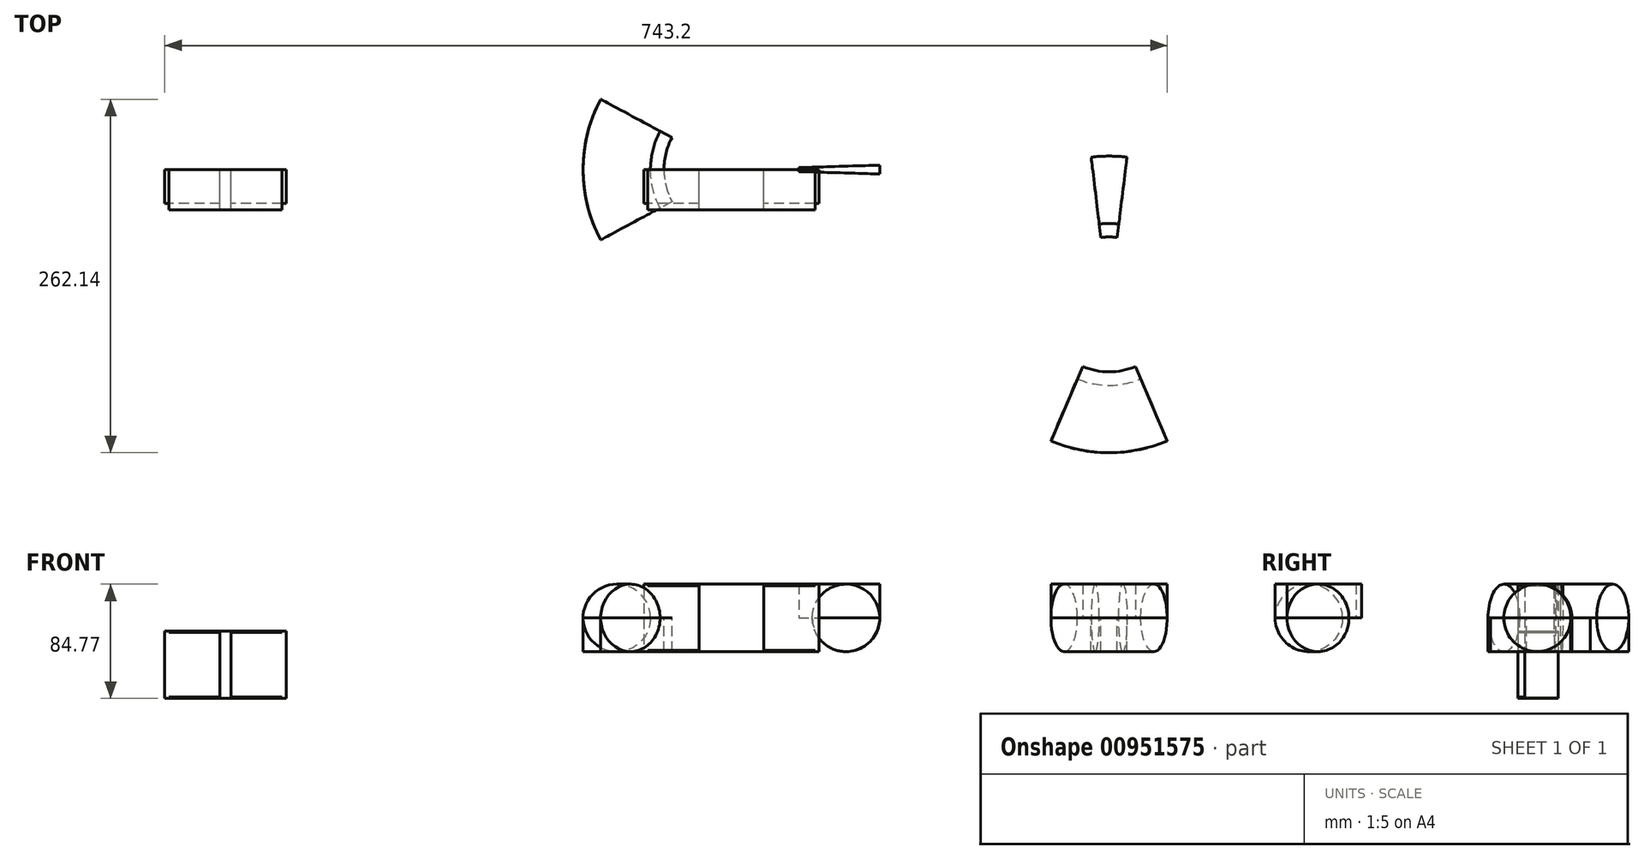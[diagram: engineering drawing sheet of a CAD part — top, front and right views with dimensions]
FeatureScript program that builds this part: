
annotation { "Feature Type Name" : "Feature", "Feature Type Description" : "" }
export const myFeature = defineFeature(function(context is Context, id is Id, definition is map)
    precondition{}
    {
        {
            var Q0;
            Q0=qCreatedBy(makeId("Top.planeOp"),FACE);
            var sketch = newSketch(context, id + "F0", { "sketchPlane" : qUnion([Q0])});
            skCircle(sketch, "E0", {"center": v(0, 0) * mm, "radius": 110 * mm});
            skLineSegment(sketch, "E1", {"start": v(0, 0) * mm, "end": v(-143.93, 0) * mm, "construction": true});
            skLineSegment(sketch, "E2", {"start": v(0, 0) * mm, "end": v(0, 124.12) * mm, "construction": true});
            skCircle(sketch, "E3", {"center": v(0, 0) * mm, "radius": 50 * mm});
            skLineSegment(sketch, "E4", {"start": v(0, 0) * mm, "end": v(109.95, 3.28) * mm});
            skLineSegment(sketch, "E5", {"start": v(0, 0) * mm, "end": v(-96.86, 52.14) * mm});
            skLineSegment(sketch, "E6", {"start": v(0, 0) * mm, "end": v(20.7, 87.59) * mm, "construction": true});
            skCircle(sketch, "E7", {"center": v(20.7, 87.59) * mm, "radius": 8 * mm});
            skCircle(sketch, "E8", {"center": v(190, 90) * mm, "radius": 23.3 * mm, "construction": true});
            skCircle(sketch, "E9", {"center": v(210.17, 101.65) * mm, "radius": 9.5 * mm});
            skLineSegment(sketch, "E10", {"start": v(20.7, 87.59) * mm, "end": v(210.17, 101.65) * mm, "construction": true});
            skLineSegment(sketch, "E11", {"start": v(210.17, 101.65) * mm, "end": v(190, 90) * mm});
            skLineSegment(sketch, "E12", {"start": v(190, -100) * mm, "end": v(280, -100) * mm, "construction": true});
            skCircle(sketch, "E13", {"center": v(280, -100) * mm, "radius": 110 * mm});
            skLineSegment(sketch, "E14", {"start": v(210.17, 101.65) * mm, "end": v(190.9, -87.37) * mm, "construction": true});
            skCircle(sketch, "E15", {"center": v(280, -100) * mm, "radius": 90 * mm, "construction": true});
            skCircle(sketch, "E16", {"center": v(0, 0) * mm, "radius": 90 * mm, "construction": true});
            skLineSegment(sketch, "E17", {"start": v(190.9, -87.37) * mm, "end": v(280, -100) * mm, "construction": true});
            skCircle(sketch, "E18", {"center": v(280, -100) * mm, "radius": 50 * mm});
            skCircle(sketch, "E19", {"center": v(20.7, 87.59) * mm, "radius": 23.3 * mm, "construction": true});
            skLineSegment(sketch, "E20", {"start": v(0, 0) * mm, "end": v(-2.51, 84.3) * mm, "construction": true});
            skLineSegment(sketch, "E21", {"start": v(0, 0) * mm, "end": v(41.46, 77.02) * mm, "construction": true});
            skCircle(sketch, "E22", {"center": v(190.9, -87.37) * mm, "radius": 23.3 * mm, "construction": true});
            skLineSegment(sketch, "E23", {"start": v(280, -100) * mm, "end": v(266.72, 9.2) * mm});
            skLineSegment(sketch, "E24", {"start": v(280, -100) * mm, "end": v(236.9, -201.2) * mm});
            skLineSegment(sketch, "E25", {"start": v(190, 90) * mm, "end": v(0, 90) * mm, "construction": true});
            skCircle(sketch, "E26", {"center": v(190.9, -87.37) * mm, "radius": 8 * mm});
            skLineSegment(sketch, "E27", {"start": v(190, 90) * mm, "end": v(190, -203.4) * mm, "construction": true});
            skLineSegment(sketch, "E28", {"start": v(0, 0) * mm, "end": v(-96.86, -52.14) * mm});
            skLineSegment(sketch, "E29", {"start": v(0, 0) * mm, "end": v(109.95, -3.28) * mm});
            skLineSegment(sketch, "E30", {"start": v(0, 0) * mm, "end": v(20.7, -87.59) * mm, "construction": true});
            skLineSegment(sketch, "E31", {"start": v(280, -100) * mm, "end": v(293.28, 9.2) * mm});
            skLineSegment(sketch, "E32", {"start": v(280, -100) * mm, "end": v(323.1, -201.2) * mm});
            skLineSegment(sketch, "E33", {"start": v(280, -100) * mm, "end": v(369.1, -87.37) * mm, "construction": true});
            skLineSegment(sketch, "E34", {"start": v(280, -100) * mm, "end": v(280, 59.02) * mm, "construction": true});
            skLineSegment(sketch, "E35", {"start": v(110, 0) * mm, "end": v(246.79, 69.95) * mm, "construction": true});
            skLineSegment(sketch, "E36", {"start": v(246.79, 69.95) * mm, "end": v(280, 10) * mm, "construction": true});
            skLineSegment(sketch, "E37", {"start": v(-110, 0) * mm, "end": v(-201, -57.62) * mm, "construction": true});
            skLineSegment(sketch, "E38", {"start": v(-201, -57.62) * mm, "end": v(-128.27, -241.78) * mm, "construction": true});
            skLineSegment(sketch, "E39", {"start": v(-128.27, -241.78) * mm, "end": v(280, -241.78) * mm, "construction": true});
            skLineSegment(sketch, "E40", {"start": v(280, -241.78) * mm, "end": v(280, -210) * mm, "construction": true});
            skSolve(sketch);
        }
        {
            var Q0;
            {var subQ0=sQuery(id+"F0.wireOp",EDGE,"E4");var subQ1=sQuery(id+"F0.wireOp",EDGE,"E0");var subQ2=makeQuery(id+"F0.imprint","INTERSECT",VERTEX,{"derivedFrom":[subQ1,subQ0]});Q0=makeQuery(id+"F0.imprint","IMPRINT",FACE,{"disambiguationData":[TD([[makeQuery(id+"F0.imprint","IMPRINT",EDGE,{"disambiguationData":[TD([[subQ2,1.0]])],"derivedFrom":subQ1}),1.0]])]});}
            var Q1;
            {var subQ0=sQuery(id+"F0.wireOp",EDGE,"E24");var subQ1=sQuery(id+"F0.wireOp",EDGE,"E13");var subQ2=makeQuery(id+"F0.imprint","INTERSECT",VERTEX,{"derivedFrom":[subQ1,subQ0]});Q1=makeQuery(id+"F0.imprint","IMPRINT",FACE,{"disambiguationData":[TD([[makeQuery(id+"F0.imprint","IMPRINT",EDGE,{"disambiguationData":[TD([[subQ2,-1.0]])],"derivedFrom":subQ1}),1.0]])]});}
            extrude(context, id + "F1", {"entities" : qUnion([Q0, Q1]), "depth" : 25 * mm, "offsetDistance" : 25 * mm});
        }
        {
            var Q0;
            {var subQ0=sQuery(id+"F0.wireOp",EDGE,"E5");var subQ1=sQuery(id+"F0.wireOp",EDGE,"E0");var subQ2=makeQuery(id+"F0.imprint","INTERSECT",VERTEX,{"derivedFrom":[subQ1,subQ0]});Q0=makeQuery(id+"F0.imprint","IMPRINT",FACE,{"disambiguationData":[TD([[makeQuery(id+"F0.imprint","IMPRINT",EDGE,{"disambiguationData":[TD([[subQ2,-1.0]])],"derivedFrom":subQ1}),1.0]])]});}
            var Q1;
            {var subQ0=sQuery(id+"F0.wireOp",EDGE,"E23");var subQ1=sQuery(id+"F0.wireOp",EDGE,"E13");var subQ2=makeQuery(id+"F0.imprint","INTERSECT",VERTEX,{"derivedFrom":[subQ1,subQ0]});Q1=makeQuery(id+"F0.imprint","IMPRINT",FACE,{"disambiguationData":[TD([[makeQuery(id+"F0.imprint","IMPRINT",EDGE,{"disambiguationData":[TD([[subQ2,1.0]])],"derivedFrom":subQ1}),1.0]])]});}
            extrude(context, id + "F2", {"entities" : qUnion([Q0, Q1]), "oppositeDirection" : true, "depth" : 25 * mm, "offsetDistance" : 25 * mm});
        }
        {
            var Q0;
            Q0=qCreatedBy(makeId("Front.planeOp"),FACE);
            var sketch = newSketch(context, id + "F3", { "sketchPlane" : qUnion([Q0])});
            skLineSegment(sketch, "E41", {"start": v(0, 0) * mm, "end": v(0, 86.34) * mm});
            skCircle(sketch, "E42", {"center": v(-85, 0) * mm, "radius": 25 * mm});
            skLineSegment(sketch, "E43", {"start": v(0, 0) * mm, "end": v(123.31, 0) * mm});
            skPoint(sketch, "E44", {"position": v(-110, 0) * mm});
            skSolve(sketch);
        }
        {
            var Q0;
            Q0=makeQuery(id+"F3.imprint","IMPRINT",FACE,{"disambiguationData":[TD([[makeQuery(id+"F3.imprint","IMPRINT",EDGE,{"derivedFrom":sQuery(id+"F3.wireOp",EDGE,"E42")}),1.0]])]});
            var Q1;
            Q1=sQuery(id+"F3.wireOp",EDGE,"E41");
            revolve(context, id + "F4", {"surfaceOperationType" : NewSurfaceOperationType.NEW, "entities" : qUnion([Q0]), "axis" : qUnion([Q1]), "revolveType" : RevolveType.FULL});
        }
        {
            var Q0;
            {var subQ0=sQuery(id+"F0.wireOp",EDGE,"E28");var subQ1=sQuery(id+"F0.wireOp",EDGE,"E0");var subQ2=makeQuery(id+"F0.imprint","INTERSECT",VERTEX,{"derivedFrom":[subQ1,subQ0]});Q0=makeQuery(id+"F0.imprint","IMPRINT",FACE,{"disambiguationData":[TD([[makeQuery(id+"F0.imprint","IMPRINT",EDGE,{"disambiguationData":[TD([[subQ2,-1.0]])],"derivedFrom":subQ1}),1.0]])]});}
            var Q1;
            Q1=makeQuery(id+"F0.imprint","IMPRINT",FACE,{"disambiguationData":[TD([[makeQuery(id+"F0.imprint","IMPRINT",EDGE,{"derivedFrom":sQuery(id+"F0.wireOp",EDGE,"E7")}),-1.0]])]});
            var Q2;
            Q2=makeQuery(id+"F0.imprint","IMPRINT",FACE,{"disambiguationData":[TD([[makeQuery(id+"F0.imprint","IMPRINT",EDGE,{"derivedFrom":sQuery(id+"F0.wireOp",EDGE,"E7")}),1.0]])]});
            extrude(context, id + "F5", {"entities" : qUnion([Q0, Q1, Q2]), "operationType" : NewBodyOperationType.REMOVE, "endBound" : BoundingType.SYMMETRIC, "depth" : 800 * mm, "offsetDistance" : 25 * mm});
        }
        {
            var Q0;
            Q0=qCreatedBy(makeId("Right.planeOp"),FACE);
            var Q1;
            Q1=sQuery(id+"F0.wireOp",VERTEX,"E36.end");
            cPlane(context, id + "F6", {"entities" : qUnion([Q0, Q1]), "cplaneType" : CPlaneType.PLANE_POINT, "offset" : 25 * mm, "width" : 150 * mm, "height" : 150 * mm});
        }
        {
            var Q0;
            Q0=qCreatedBy(id+"F6.planeOp",FACE);
            var sketch = newSketch(context, id + "F7", { "sketchPlane" : qUnion([Q0])});
            skLineSegment(sketch, "E45", {"start": v(-100, 70.8) * mm, "end": v(-100, 0) * mm});
            skCircle(sketch, "E46", {"center": v(-15, 0) * mm, "radius": 25 * mm});
            skLineSegment(sketch, "E47", {"start": v(-15, 0) * mm, "end": v(10, 0) * mm, "construction": true});
            skLineSegment(sketch, "E48", {"start": v(-100, 0) * mm, "end": v(-330.04, 0) * mm});
            skSolve(sketch);
        }
        {
            var Q0;
            Q0=makeQuery(id+"F7.imprint","IMPRINT",FACE,{"disambiguationData":[TD([[makeQuery(id+"F7.imprint","IMPRINT",EDGE,{"derivedFrom":sQuery(id+"F7.wireOp",EDGE,"E46")}),1.0]])]});
            var Q1;
            Q1=sQuery(id+"F7.wireOp",EDGE,"E45");
            revolve(context, id + "F8", {"surfaceOperationType" : NewSurfaceOperationType.NEW, "entities" : qUnion([Q0]), "axis" : qUnion([Q1]), "revolveType" : RevolveType.FULL});
        }
        {
            var Q0;
            {var subQ0=sQuery(id+"F0.wireOp",EDGE,"E31");var subQ1=sQuery(id+"F0.wireOp",EDGE,"E13");var subQ2=makeQuery(id+"F0.imprint","INTERSECT",VERTEX,{"derivedFrom":[subQ1,subQ0]});Q0=makeQuery(id+"F0.imprint","IMPRINT",FACE,{"disambiguationData":[TD([[makeQuery(id+"F0.imprint","IMPRINT",EDGE,{"disambiguationData":[TD([[subQ2,1.0]])],"derivedFrom":subQ1}),1.0]])]});}
            var Q1;
            Q1=makeQuery(id+"F0.imprint","IMPRINT",FACE,{"disambiguationData":[TD([[makeQuery(id+"F0.imprint","IMPRINT",EDGE,{"derivedFrom":sQuery(id+"F0.wireOp",EDGE,"E26")}),-1.0]])]});
            var Q2;
            Q2=makeQuery(id+"F0.imprint","IMPRINT",FACE,{"disambiguationData":[TD([[makeQuery(id+"F0.imprint","IMPRINT",EDGE,{"derivedFrom":sQuery(id+"F0.wireOp",EDGE,"E26")}),1.0]])]});
            extrude(context, id + "F9", {"entities" : qUnion([Q0, Q1, Q2]), "operationType" : NewBodyOperationType.REMOVE, "endBound" : BoundingType.SYMMETRIC, "depth" : 800 * mm, "offsetDistance" : 25 * mm});
        }
        {
            var Q0;
            Q0=qCreatedBy(makeId("Front.planeOp"),FACE);
            var sketch = newSketch(context, id + "F10", { "sketchPlane" : qUnion([Q0])});
            skLineSegment(sketch, "E49.bottom", {"start": v(-65, 25) * mm, "end": v(65, 25) * mm});
            skLineSegment(sketch, "E49.top", {"start": v(-65, -25) * mm, "end": v(65, -25) * mm});
            skLineSegment(sketch, "E49.left", {"start": v(-65, 25) * mm, "end": v(-65, -25) * mm});
            skLineSegment(sketch, "E49.right", {"start": v(65, 25) * mm, "end": v(65, -25) * mm});
            skPoint(sketch, "E49.middle", {"position": v(0, 0) * mm});
            skLineSegment(sketch, "E50", {"start": v(-62, 25) * mm, "end": v(-62, 24) * mm});
            skLineSegment(sketch, "E51", {"start": v(-62, 24) * mm, "end": v(-24, 24) * mm});
            skLineSegment(sketch, "E52", {"start": v(-24, 24) * mm, "end": v(-24, -24) * mm});
            skLineSegment(sketch, "E53", {"start": v(0, 0) * mm, "end": v(40.86, 0) * mm});
            skLineSegment(sketch, "E54", {"start": v(0, 0) * mm, "end": v(0, 32.58) * mm});
            skLineSegment(sketch, "E55", {"start": v(-24, -24) * mm, "end": v(-62, -24) * mm});
            skLineSegment(sketch, "E56", {"start": v(-62, -24) * mm, "end": v(-62, -25) * mm});
            skLineSegment(sketch, "E57.MirrorCS", {"start": v(62, 25) * mm, "end": v(62, 24) * mm});
            skLineSegment(sketch, "E58.MirrorCS", {"start": v(62, 24) * mm, "end": v(24, 24) * mm});
            skLineSegment(sketch, "E59.MirrorCS", {"start": v(24, 24) * mm, "end": v(24, -24) * mm});
            skLineSegment(sketch, "E60.MirrorCS", {"start": v(24, -24) * mm, "end": v(62, -24) * mm});
            skLineSegment(sketch, "E61.MirrorCS", {"start": v(62, -24) * mm, "end": v(62, -25) * mm});
            skLineSegment(sketch, "E62", {"start": v(0, 29.12) * mm, "end": v(-2.43, 29.12) * mm});
            skLineSegment(sketch, "E63", {"start": v(-3, 40) * mm, "end": v(-4, 40) * mm});
            skLineSegment(sketch, "E64", {"start": v(-4, 40) * mm, "end": v(-4.57, 29.12) * mm});
            skLineSegment(sketch, "E65", {"start": v(-3.5, 43.91) * mm, "end": v(-3.5, 28.26) * mm, "construction": true});
            skPoint(sketch, "E66.orphan", {"position": v(-3.5, 40) * mm});
            skLineSegment(sketch, "E67.MirrorCS", {"start": v(-3, 40) * mm, "end": v(-2.43, 29.12) * mm});
            skLineSegment(sketch, "E68", {"start": v(-4.57, 29.12) * mm, "end": v(-7, 29.12) * mm});
            skPoint(sketch, "E69.1.0.0", {"position": v(-10.5, 40) * mm});
            skLineSegment(sketch, "E69.1.0.1", {"start": v(-10.5, 43.91) * mm, "end": v(-10.5, 28.26) * mm, "construction": true});
            skLineSegment(sketch, "E69.1.0.2", {"start": v(-11, 40) * mm, "end": v(-11.57, 29.12) * mm});
            skLineSegment(sketch, "E69.1.0.3", {"start": v(-10, 40) * mm, "end": v(-9.43, 29.12) * mm});
            skLineSegment(sketch, "E69.1.0.4", {"start": v(-11.57, 29.12) * mm, "end": v(-14, 29.12) * mm});
            skLineSegment(sketch, "E69.1.0.5", {"start": v(-7, 29.12) * mm, "end": v(-9.43, 29.12) * mm});
            skLineSegment(sketch, "E69.1.0.6", {"start": v(-10, 40) * mm, "end": v(-11, 40) * mm});
            skLineSegment(sketch, "E69.1.0.7", {"start": v(-72, 25) * mm, "end": v(58, 25) * mm});
            skPoint(sketch, "E69.2.0.0", {"position": v(-17.5, 40) * mm});
            skLineSegment(sketch, "E69.2.0.1", {"start": v(-17.5, 43.91) * mm, "end": v(-17.5, 28.26) * mm, "construction": true});
            skLineSegment(sketch, "E69.2.0.2", {"start": v(-18, 40) * mm, "end": v(-18.57, 29.12) * mm});
            skLineSegment(sketch, "E69.2.0.3", {"start": v(-17, 40) * mm, "end": v(-16.43, 29.12) * mm});
            skLineSegment(sketch, "E69.2.0.4", {"start": v(-18.57, 29.12) * mm, "end": v(-21, 29.12) * mm});
            skLineSegment(sketch, "E69.2.0.5", {"start": v(-14, 29.12) * mm, "end": v(-16.43, 29.12) * mm});
            skLineSegment(sketch, "E69.2.0.6", {"start": v(-17, 40) * mm, "end": v(-18, 40) * mm});
            skLineSegment(sketch, "E69.2.0.7", {"start": v(-79, 25) * mm, "end": v(51, 25) * mm});
            skPoint(sketch, "E69.3.0.0", {"position": v(-24.5, 40) * mm});
            skLineSegment(sketch, "E69.3.0.1", {"start": v(-24.5, 43.91) * mm, "end": v(-24.5, 28.26) * mm, "construction": true});
            skLineSegment(sketch, "E69.3.0.2", {"start": v(-25, 40) * mm, "end": v(-25.57, 29.12) * mm});
            skLineSegment(sketch, "E69.3.0.3", {"start": v(-24, 40) * mm, "end": v(-23.43, 29.12) * mm});
            skLineSegment(sketch, "E69.3.0.4", {"start": v(-25.57, 29.12) * mm, "end": v(-28, 29.12) * mm});
            skLineSegment(sketch, "E69.3.0.5", {"start": v(-21, 29.12) * mm, "end": v(-23.43, 29.12) * mm});
            skLineSegment(sketch, "E69.3.0.6", {"start": v(-24, 40) * mm, "end": v(-25, 40) * mm});
            skLineSegment(sketch, "E69.3.0.7", {"start": v(-86, 25) * mm, "end": v(44, 25) * mm});
            skPoint(sketch, "E69.4.0.0", {"position": v(-31.5, 40) * mm});
            skLineSegment(sketch, "E69.4.0.1", {"start": v(-31.5, 43.91) * mm, "end": v(-31.5, 28.26) * mm, "construction": true});
            skLineSegment(sketch, "E69.4.0.2", {"start": v(-32, 40) * mm, "end": v(-32.57, 29.12) * mm});
            skLineSegment(sketch, "E69.4.0.3", {"start": v(-31, 40) * mm, "end": v(-30.43, 29.12) * mm});
            skLineSegment(sketch, "E69.4.0.4", {"start": v(-32.57, 29.12) * mm, "end": v(-35, 29.12) * mm});
            skLineSegment(sketch, "E69.4.0.5", {"start": v(-28, 29.12) * mm, "end": v(-30.43, 29.12) * mm});
            skLineSegment(sketch, "E69.4.0.6", {"start": v(-31, 40) * mm, "end": v(-32, 40) * mm});
            skLineSegment(sketch, "E69.4.0.7", {"start": v(-93, 25) * mm, "end": v(37, 25) * mm});
            skPoint(sketch, "E69.5.0.0", {"position": v(-38.5, 40) * mm});
            skLineSegment(sketch, "E69.5.0.1", {"start": v(-38.5, 43.91) * mm, "end": v(-38.5, 28.26) * mm, "construction": true});
            skLineSegment(sketch, "E69.5.0.2", {"start": v(-39, 40) * mm, "end": v(-39.57, 29.12) * mm});
            skLineSegment(sketch, "E69.5.0.3", {"start": v(-38, 40) * mm, "end": v(-37.43, 29.12) * mm});
            skLineSegment(sketch, "E69.5.0.4", {"start": v(-39.57, 29.12) * mm, "end": v(-42, 29.12) * mm});
            skLineSegment(sketch, "E69.5.0.5", {"start": v(-35, 29.12) * mm, "end": v(-37.43, 29.12) * mm});
            skLineSegment(sketch, "E69.5.0.6", {"start": v(-38, 40) * mm, "end": v(-39, 40) * mm});
            skLineSegment(sketch, "E69.5.0.7", {"start": v(-100, 25) * mm, "end": v(30, 25) * mm});
            skPoint(sketch, "E69.6.0.0", {"position": v(-45.5, 40) * mm});
            skLineSegment(sketch, "E69.6.0.1", {"start": v(-45.5, 43.91) * mm, "end": v(-45.5, 28.26) * mm, "construction": true});
            skLineSegment(sketch, "E69.6.0.2", {"start": v(-46, 40) * mm, "end": v(-46.57, 29.12) * mm});
            skLineSegment(sketch, "E69.6.0.3", {"start": v(-45, 40) * mm, "end": v(-44.43, 29.12) * mm});
            skLineSegment(sketch, "E69.6.0.4", {"start": v(-46.57, 29.12) * mm, "end": v(-49, 29.12) * mm});
            skLineSegment(sketch, "E69.6.0.5", {"start": v(-42, 29.12) * mm, "end": v(-44.43, 29.12) * mm});
            skLineSegment(sketch, "E69.6.0.6", {"start": v(-45, 40) * mm, "end": v(-46, 40) * mm});
            skLineSegment(sketch, "E69.6.0.7", {"start": v(-107, 25) * mm, "end": v(23, 25) * mm});
            skLineSegment(sketch, "E69.direction1", {"start": v(-7, 29.12) * mm, "end": v(-14, 29.12) * mm, "construction": true});
            skLineSegment(sketch, "E70.MirrorCS", {"start": v(4.57, 29.12) * mm, "end": v(7, 29.12) * mm});
            skLineSegment(sketch, "E71.MirrorCS", {"start": v(7, 29.12) * mm, "end": v(9.43, 29.12) * mm});
            skLineSegment(sketch, "E72.MirrorCS", {"start": v(42, 29.12) * mm, "end": v(44.43, 29.12) * mm});
            skLineSegment(sketch, "E73.MirrorCS", {"start": v(39.57, 29.12) * mm, "end": v(42, 29.12) * mm});
            skLineSegment(sketch, "E74.MirrorCS", {"start": v(32.57, 29.12) * mm, "end": v(35, 29.12) * mm});
            skLineSegment(sketch, "E75.MirrorCS", {"start": v(45, 40) * mm, "end": v(46, 40) * mm});
            skLineSegment(sketch, "E76.MirrorCS", {"start": v(11.57, 29.12) * mm, "end": v(14, 29.12) * mm});
            skLineSegment(sketch, "E77.MirrorCS", {"start": v(24, 40) * mm, "end": v(25, 40) * mm});
            skLineSegment(sketch, "E78.MirrorCS", {"start": v(10, 40) * mm, "end": v(11, 40) * mm});
            skLineSegment(sketch, "E79.MirrorCS", {"start": v(18.57, 29.12) * mm, "end": v(21, 29.12) * mm});
            skLineSegment(sketch, "E80.MirrorCS", {"start": v(31, 40) * mm, "end": v(32, 40) * mm});
            skLineSegment(sketch, "E81.MirrorCS", {"start": v(21, 29.12) * mm, "end": v(23.43, 29.12) * mm});
            skLineSegment(sketch, "E82.MirrorCS", {"start": v(3, 40) * mm, "end": v(4, 40) * mm});
            skLineSegment(sketch, "E83.MirrorCS", {"start": v(35, 29.12) * mm, "end": v(37.43, 29.12) * mm});
            skLineSegment(sketch, "E84.MirrorCS", {"start": v(14, 29.12) * mm, "end": v(16.43, 29.12) * mm});
            skLineSegment(sketch, "E85.MirrorCS", {"start": v(17, 40) * mm, "end": v(18, 40) * mm});
            skLineSegment(sketch, "E86.MirrorCS", {"start": v(38, 40) * mm, "end": v(39, 40) * mm});
            skLineSegment(sketch, "E87.MirrorCS", {"start": v(28, 29.12) * mm, "end": v(30.43, 29.12) * mm});
            skLineSegment(sketch, "E88.MirrorCS", {"start": v(46.57, 29.12) * mm, "end": v(49, 29.12) * mm});
            skLineSegment(sketch, "E89.MirrorCS", {"start": v(0, 29.12) * mm, "end": v(2.43, 29.12) * mm});
            skLineSegment(sketch, "E90.MirrorCS", {"start": v(7, 29.12) * mm, "end": v(14, 29.12) * mm, "construction": true});
            skLineSegment(sketch, "E91.MirrorCS", {"start": v(25.57, 29.12) * mm, "end": v(28, 29.12) * mm});
            skLineSegment(sketch, "E92.MirrorCS", {"start": v(3.5, 43.91) * mm, "end": v(3.5, 28.26) * mm, "construction": true});
            skLineSegment(sketch, "E93.MirrorCS", {"start": v(17, 40) * mm, "end": v(16.43, 29.12) * mm});
            skLineSegment(sketch, "E94.MirrorCS", {"start": v(39, 40) * mm, "end": v(39.57, 29.12) * mm});
            skPoint(sketch, "E95.MirrorP", {"position": v(10.5, 40) * mm});
            skLineSegment(sketch, "E96.MirrorCS", {"start": v(3, 40) * mm, "end": v(2.43, 29.12) * mm});
            skLineSegment(sketch, "E97.MirrorCS", {"start": v(17.5, 43.91) * mm, "end": v(17.5, 28.26) * mm, "construction": true});
            skLineSegment(sketch, "E98.MirrorCS", {"start": v(24.5, 43.91) * mm, "end": v(24.5, 28.26) * mm, "construction": true});
            skLineSegment(sketch, "E99.MirrorCS", {"start": v(38, 40) * mm, "end": v(37.43, 29.12) * mm});
            skLineSegment(sketch, "E100.MirrorCS", {"start": v(31, 40) * mm, "end": v(30.43, 29.12) * mm});
            skPoint(sketch, "E101.MirrorP", {"position": v(17.5, 40) * mm});
            skLineSegment(sketch, "E102.MirrorCS", {"start": v(18, 40) * mm, "end": v(18.57, 29.12) * mm});
            skLineSegment(sketch, "E103.MirrorCS", {"start": v(25, 40) * mm, "end": v(25.57, 29.12) * mm});
            skPoint(sketch, "E104.MirrorP", {"position": v(24.5, 40) * mm});
            skLineSegment(sketch, "E105.MirrorCS", {"start": v(46, 40) * mm, "end": v(46.57, 29.12) * mm});
            skLineSegment(sketch, "E106.MirrorCS", {"start": v(45, 40) * mm, "end": v(44.43, 29.12) * mm});
            skLineSegment(sketch, "E107.MirrorCS", {"start": v(31.5, 43.91) * mm, "end": v(31.5, 28.26) * mm, "construction": true});
            skLineSegment(sketch, "E108.MirrorCS", {"start": v(32, 40) * mm, "end": v(32.57, 29.12) * mm});
            skPoint(sketch, "E109.MirrorP", {"position": v(45.5, 40) * mm});
            skLineSegment(sketch, "E110.MirrorCS", {"start": v(10.5, 43.91) * mm, "end": v(10.5, 28.26) * mm, "construction": true});
            skPoint(sketch, "E111.MirrorP", {"position": v(31.5, 40) * mm});
            skLineSegment(sketch, "E112.MirrorCS", {"start": v(10, 40) * mm, "end": v(9.43, 29.12) * mm});
            skLineSegment(sketch, "E113.MirrorCS", {"start": v(11, 40) * mm, "end": v(11.57, 29.12) * mm});
            skLineSegment(sketch, "E114.MirrorCS", {"start": v(38.5, 43.91) * mm, "end": v(38.5, 28.26) * mm, "construction": true});
            skPoint(sketch, "E115.MirrorP", {"position": v(38.5, 40) * mm});
            skLineSegment(sketch, "E116.MirrorCS", {"start": v(4, 40) * mm, "end": v(4.57, 29.12) * mm});
            skLineSegment(sketch, "E117.MirrorCS", {"start": v(45.5, 43.91) * mm, "end": v(45.5, 28.26) * mm, "construction": true});
            skPoint(sketch, "E118.MirrorP", {"position": v(3.5, 40) * mm});
            skLineSegment(sketch, "E119.MirrorCS", {"start": v(24, 40) * mm, "end": v(23.43, 29.12) * mm});
            skLineSegment(sketch, "E120", {"start": v(65, 25) * mm, "end": v(80, 25) * mm});
            skLineSegment(sketch, "E121", {"start": v(-65, 25) * mm, "end": v(-49, 25) * mm});
            skLineSegment(sketch, "E122", {"start": v(80, 25) * mm, "end": v(80, 29.12) * mm});
            skLineSegment(sketch, "E123", {"start": v(80, 29.12) * mm, "end": v(49, 29.12) * mm});
            skLineSegment(sketch, "E124", {"start": v(-49, 29.12) * mm, "end": v(-80, 29.12) * mm});
            skLineSegment(sketch, "E125", {"start": v(-80, 29.12) * mm, "end": v(-80, 25) * mm});
            skLineSegment(sketch, "E126.bottom", {"start": v(-420.1, -9.77) * mm, "end": v(-330.1, -9.77) * mm});
            skLineSegment(sketch, "E126.top", {"start": v(-420.1, -59.77) * mm, "end": v(-330.1, -59.77) * mm});
            skLineSegment(sketch, "E126.left", {"start": v(-420.1, -9.77) * mm, "end": v(-420.1, -59.77) * mm});
            skLineSegment(sketch, "E126.right", {"start": v(-330.1, -9.77) * mm, "end": v(-330.1, -59.77) * mm});
            skPoint(sketch, "E126.middle", {"position": v(-375.1, -34.77) * mm});
            skLineSegment(sketch, "E127", {"start": v(-417.1, -9.77) * mm, "end": v(-417.1, -10.77) * mm});
            skLineSegment(sketch, "E128", {"start": v(-417.1, -10.77) * mm, "end": v(-379.1, -10.77) * mm});
            skLineSegment(sketch, "E129", {"start": v(-379.1, -10.77) * mm, "end": v(-379.1, -58.77) * mm});
            skLineSegment(sketch, "E130", {"start": v(-375.1, -34.77) * mm, "end": v(-354.24, -34.77) * mm});
            skLineSegment(sketch, "E131", {"start": v(-375.1, -34.77) * mm, "end": v(-375.1, -2.18) * mm});
            skLineSegment(sketch, "E132", {"start": v(-379.1, -58.77) * mm, "end": v(-417.1, -58.77) * mm});
            skLineSegment(sketch, "E133", {"start": v(-417.1, -58.77) * mm, "end": v(-417.1, -59.77) * mm});
            skLineSegment(sketch, "E134.MirrorCS", {"start": v(-333.1, -9.77) * mm, "end": v(-333.1, -10.77) * mm});
            skLineSegment(sketch, "E135.MirrorCS", {"start": v(-333.1, -10.77) * mm, "end": v(-371.1, -10.77) * mm});
            skLineSegment(sketch, "E136.MirrorCS", {"start": v(-371.1, -10.77) * mm, "end": v(-371.1, -58.77) * mm});
            skLineSegment(sketch, "E137.MirrorCS", {"start": v(-371.1, -58.77) * mm, "end": v(-333.1, -58.77) * mm});
            skLineSegment(sketch, "E138.MirrorCS", {"start": v(-333.1, -58.77) * mm, "end": v(-333.1, -59.77) * mm});
            skLineSegment(sketch, "E139", {"start": v(-375.1, -5.65) * mm, "end": v(-377.53, -5.65) * mm});
            skLineSegment(sketch, "E140", {"start": v(-378.1, 5.23) * mm, "end": v(-379.1, 5.23) * mm});
            skLineSegment(sketch, "E141", {"start": v(-379.1, 5.23) * mm, "end": v(-379.67, -5.65) * mm});
            skLineSegment(sketch, "E142", {"start": v(-378.6, 9.15) * mm, "end": v(-378.6, -6.5) * mm, "construction": true});
            skPoint(sketch, "E143.orphan", {"position": v(-378.6, 5.23) * mm});
            skLineSegment(sketch, "E144.MirrorCS", {"start": v(-378.1, 5.23) * mm, "end": v(-377.53, -5.65) * mm});
            skLineSegment(sketch, "E145", {"start": v(-379.67, -5.65) * mm, "end": v(-382.1, -5.65) * mm});
            skPoint(sketch, "E146.1.0.0", {"position": v(-385.6, 5.23) * mm});
            skLineSegment(sketch, "E146.1.0.1", {"start": v(-385.6, 9.15) * mm, "end": v(-385.6, -6.5) * mm, "construction": true});
            skLineSegment(sketch, "E146.1.0.2", {"start": v(-386.1, 5.23) * mm, "end": v(-386.67, -5.65) * mm});
            skLineSegment(sketch, "E146.1.0.3", {"start": v(-385.1, 5.23) * mm, "end": v(-384.53, -5.65) * mm});
            skLineSegment(sketch, "E146.1.0.4", {"start": v(-386.67, -5.65) * mm, "end": v(-389.1, -5.65) * mm});
            skLineSegment(sketch, "E146.1.0.5", {"start": v(-382.1, -5.65) * mm, "end": v(-384.53, -5.65) * mm});
            skLineSegment(sketch, "E146.1.0.6", {"start": v(-385.1, 5.23) * mm, "end": v(-386.1, 5.23) * mm});
            skLineSegment(sketch, "E146.1.0.7", {"start": v(-427.1, -9.77) * mm, "end": v(-297.1, -9.77) * mm});
            skPoint(sketch, "E146.2.0.0", {"position": v(-392.6, 5.23) * mm});
            skLineSegment(sketch, "E146.2.0.1", {"start": v(-392.6, 9.15) * mm, "end": v(-392.6, -6.5) * mm, "construction": true});
            skLineSegment(sketch, "E146.2.0.2", {"start": v(-393.1, 5.23) * mm, "end": v(-393.67, -5.65) * mm});
            skLineSegment(sketch, "E146.2.0.3", {"start": v(-392.1, 5.23) * mm, "end": v(-391.53, -5.65) * mm});
            skLineSegment(sketch, "E146.2.0.4", {"start": v(-393.67, -5.65) * mm, "end": v(-396.1, -5.65) * mm});
            skLineSegment(sketch, "E146.2.0.5", {"start": v(-389.1, -5.65) * mm, "end": v(-391.53, -5.65) * mm});
            skLineSegment(sketch, "E146.2.0.6", {"start": v(-392.1, 5.23) * mm, "end": v(-393.1, 5.23) * mm});
            skLineSegment(sketch, "E146.2.0.7", {"start": v(-454.1, -9.77) * mm, "end": v(-324.1, -9.77) * mm});
            skPoint(sketch, "E146.3.0.0", {"position": v(-399.6, 5.23) * mm});
            skLineSegment(sketch, "E146.3.0.1", {"start": v(-399.6, 9.15) * mm, "end": v(-399.6, -6.5) * mm, "construction": true});
            skLineSegment(sketch, "E146.3.0.2", {"start": v(-400.1, 5.23) * mm, "end": v(-400.67, -5.65) * mm});
            skLineSegment(sketch, "E146.3.0.3", {"start": v(-399.1, 5.23) * mm, "end": v(-398.53, -5.65) * mm});
            skLineSegment(sketch, "E146.3.0.4", {"start": v(-400.67, -5.65) * mm, "end": v(-403.1, -5.65) * mm});
            skLineSegment(sketch, "E146.3.0.5", {"start": v(-396.1, -5.65) * mm, "end": v(-398.53, -5.65) * mm});
            skLineSegment(sketch, "E146.3.0.6", {"start": v(-399.1, 5.23) * mm, "end": v(-400.1, 5.23) * mm});
            skLineSegment(sketch, "E146.3.0.7", {"start": v(-461.1, -9.77) * mm, "end": v(-331.1, -9.77) * mm});
            skPoint(sketch, "E146.4.0.0", {"position": v(-406.6, 5.23) * mm});
            skLineSegment(sketch, "E146.4.0.1", {"start": v(-406.6, 9.15) * mm, "end": v(-406.6, -6.5) * mm, "construction": true});
            skLineSegment(sketch, "E146.4.0.2", {"start": v(-407.1, 5.23) * mm, "end": v(-407.67, -5.65) * mm});
            skLineSegment(sketch, "E146.4.0.3", {"start": v(-406.1, 5.23) * mm, "end": v(-405.53, -5.65) * mm});
            skLineSegment(sketch, "E146.4.0.4", {"start": v(-407.67, -5.65) * mm, "end": v(-410.1, -5.65) * mm});
            skLineSegment(sketch, "E146.4.0.5", {"start": v(-403.1, -5.65) * mm, "end": v(-405.53, -5.65) * mm});
            skLineSegment(sketch, "E146.4.0.6", {"start": v(-406.1, 5.23) * mm, "end": v(-407.1, 5.23) * mm});
            skPoint(sketch, "E146.5.0.0", {"position": v(-413.6, 5.23) * mm});
            skLineSegment(sketch, "E146.5.0.1", {"start": v(-413.6, 9.15) * mm, "end": v(-413.6, -6.5) * mm, "construction": true});
            skLineSegment(sketch, "E146.5.0.2", {"start": v(-414.1, 5.23) * mm, "end": v(-414.67, -5.65) * mm});
            skLineSegment(sketch, "E146.5.0.3", {"start": v(-413.1, 5.23) * mm, "end": v(-412.53, -5.65) * mm});
            skLineSegment(sketch, "E146.5.0.4", {"start": v(-414.67, -5.65) * mm, "end": v(-417.1, -5.65) * mm});
            skLineSegment(sketch, "E146.5.0.5", {"start": v(-410.1, -5.65) * mm, "end": v(-412.53, -5.65) * mm});
            skLineSegment(sketch, "E146.5.0.6", {"start": v(-413.1, 5.23) * mm, "end": v(-414.1, 5.23) * mm});
            skPoint(sketch, "E146.6.0.0", {"position": v(-420.6, 5.23) * mm});
            skLineSegment(sketch, "E146.6.0.1", {"start": v(-420.6, 9.15) * mm, "end": v(-420.6, -6.5) * mm, "construction": true});
            skLineSegment(sketch, "E146.6.0.2", {"start": v(-421.1, 5.23) * mm, "end": v(-421.67, -5.65) * mm});
            skLineSegment(sketch, "E146.6.0.3", {"start": v(-420.1, 5.23) * mm, "end": v(-419.53, -5.65) * mm});
            skLineSegment(sketch, "E146.6.0.4", {"start": v(-421.67, -5.65) * mm, "end": v(-424.1, -5.65) * mm});
            skLineSegment(sketch, "E146.6.0.5", {"start": v(-417.1, -5.65) * mm, "end": v(-419.53, -5.65) * mm});
            skLineSegment(sketch, "E146.6.0.6", {"start": v(-420.1, 5.23) * mm, "end": v(-421.1, 5.23) * mm});
            skLineSegment(sketch, "E146.direction1", {"start": v(-382.1, -5.65) * mm, "end": v(-389.1, -5.65) * mm, "construction": true});
            skLineSegment(sketch, "E147.MirrorCS", {"start": v(-370.53, -5.65) * mm, "end": v(-368.1, -5.65) * mm});
            skLineSegment(sketch, "E148.MirrorCS", {"start": v(-368.1, -5.65) * mm, "end": v(-365.67, -5.65) * mm});
            skLineSegment(sketch, "E149.MirrorCS", {"start": v(-333.1, -5.65) * mm, "end": v(-330.67, -5.65) * mm});
            skLineSegment(sketch, "E150.MirrorCS", {"start": v(-335.53, -5.65) * mm, "end": v(-333.1, -5.65) * mm});
            skLineSegment(sketch, "E151.MirrorCS", {"start": v(-342.53, -5.65) * mm, "end": v(-340.1, -5.65) * mm});
            skLineSegment(sketch, "E152.MirrorCS", {"start": v(-330.1, 5.23) * mm, "end": v(-329.1, 5.23) * mm});
            skLineSegment(sketch, "E153.MirrorCS", {"start": v(-363.53, -5.65) * mm, "end": v(-361.1, -5.65) * mm});
            skLineSegment(sketch, "E154.MirrorCS", {"start": v(-351.1, 5.23) * mm, "end": v(-350.1, 5.23) * mm});
            skLineSegment(sketch, "E155.MirrorCS", {"start": v(-365.1, 5.23) * mm, "end": v(-364.1, 5.23) * mm});
            skLineSegment(sketch, "E156.MirrorCS", {"start": v(-356.53, -5.65) * mm, "end": v(-354.1, -5.65) * mm});
            skLineSegment(sketch, "E157.MirrorCS", {"start": v(-344.1, 5.23) * mm, "end": v(-343.1, 5.23) * mm});
            skLineSegment(sketch, "E158.MirrorCS", {"start": v(-354.1, -5.65) * mm, "end": v(-351.67, -5.65) * mm});
            skLineSegment(sketch, "E159.MirrorCS", {"start": v(-372.1, 5.23) * mm, "end": v(-371.1, 5.23) * mm});
            skLineSegment(sketch, "E160.MirrorCS", {"start": v(-340.1, -5.65) * mm, "end": v(-337.67, -5.65) * mm});
            skLineSegment(sketch, "E161.MirrorCS", {"start": v(-361.1, -5.65) * mm, "end": v(-358.67, -5.65) * mm});
            skLineSegment(sketch, "E162.MirrorCS", {"start": v(-358.1, 5.23) * mm, "end": v(-357.1, 5.23) * mm});
            skLineSegment(sketch, "E163.MirrorCS", {"start": v(-337.1, 5.23) * mm, "end": v(-336.1, 5.23) * mm});
            skLineSegment(sketch, "E164.MirrorCS", {"start": v(-347.1, -5.65) * mm, "end": v(-344.67, -5.65) * mm});
            skLineSegment(sketch, "E165.MirrorCS", {"start": v(-328.53, -5.65) * mm, "end": v(-326.1, -5.65) * mm});
            skLineSegment(sketch, "E166.MirrorCS", {"start": v(-375.1, -5.65) * mm, "end": v(-372.67, -5.65) * mm});
            skLineSegment(sketch, "E167.MirrorCS", {"start": v(-368.1, -5.65) * mm, "end": v(-361.1, -5.65) * mm, "construction": true});
            skLineSegment(sketch, "E168.MirrorCS", {"start": v(-349.53, -5.65) * mm, "end": v(-347.1, -5.65) * mm});
            skLineSegment(sketch, "E169.MirrorCS", {"start": v(-371.6, 9.15) * mm, "end": v(-371.6, -6.5) * mm, "construction": true});
            skLineSegment(sketch, "E170.MirrorCS", {"start": v(-358.1, 5.23) * mm, "end": v(-358.67, -5.65) * mm});
            skLineSegment(sketch, "E171.MirrorCS", {"start": v(-336.1, 5.23) * mm, "end": v(-335.53, -5.65) * mm});
            skPoint(sketch, "E172.MirrorP", {"position": v(-364.6, 5.23) * mm});
            skLineSegment(sketch, "E173.MirrorCS", {"start": v(-372.1, 5.23) * mm, "end": v(-372.67, -5.65) * mm});
            skLineSegment(sketch, "E174.MirrorCS", {"start": v(-357.6, 9.15) * mm, "end": v(-357.6, -6.5) * mm, "construction": true});
            skLineSegment(sketch, "E175.MirrorCS", {"start": v(-350.6, 9.15) * mm, "end": v(-350.6, -6.5) * mm, "construction": true});
            skLineSegment(sketch, "E176.MirrorCS", {"start": v(-337.1, 5.23) * mm, "end": v(-337.67, -5.65) * mm});
            skLineSegment(sketch, "E177.MirrorCS", {"start": v(-344.1, 5.23) * mm, "end": v(-344.67, -5.65) * mm});
            skPoint(sketch, "E178.MirrorP", {"position": v(-357.6, 5.23) * mm});
            skLineSegment(sketch, "E179.MirrorCS", {"start": v(-357.1, 5.23) * mm, "end": v(-356.53, -5.65) * mm});
            skLineSegment(sketch, "E180.MirrorCS", {"start": v(-350.1, 5.23) * mm, "end": v(-349.53, -5.65) * mm});
            skPoint(sketch, "E181.MirrorP", {"position": v(-350.6, 5.23) * mm});
            skLineSegment(sketch, "E182.MirrorCS", {"start": v(-329.1, 5.23) * mm, "end": v(-328.53, -5.65) * mm});
            skLineSegment(sketch, "E183.MirrorCS", {"start": v(-330.1, 5.23) * mm, "end": v(-330.67, -5.65) * mm});
            skLineSegment(sketch, "E184.MirrorCS", {"start": v(-343.6, 9.15) * mm, "end": v(-343.6, -6.5) * mm, "construction": true});
            skLineSegment(sketch, "E185.MirrorCS", {"start": v(-343.1, 5.23) * mm, "end": v(-342.53, -5.65) * mm});
            skPoint(sketch, "E186.MirrorP", {"position": v(-329.6, 5.23) * mm});
            skLineSegment(sketch, "E187.MirrorCS", {"start": v(-364.6, 9.15) * mm, "end": v(-364.6, -6.5) * mm, "construction": true});
            skPoint(sketch, "E188.MirrorP", {"position": v(-343.6, 5.23) * mm});
            skLineSegment(sketch, "E189.MirrorCS", {"start": v(-365.1, 5.23) * mm, "end": v(-365.67, -5.65) * mm});
            skLineSegment(sketch, "E190.MirrorCS", {"start": v(-364.1, 5.23) * mm, "end": v(-363.53, -5.65) * mm});
            skLineSegment(sketch, "E191.MirrorCS", {"start": v(-336.6, 9.15) * mm, "end": v(-336.6, -6.5) * mm, "construction": true});
            skPoint(sketch, "E192.MirrorP", {"position": v(-336.6, 5.23) * mm});
            skLineSegment(sketch, "E193.MirrorCS", {"start": v(-371.1, 5.23) * mm, "end": v(-370.53, -5.65) * mm});
            skLineSegment(sketch, "E194.MirrorCS", {"start": v(-329.6, 9.15) * mm, "end": v(-329.6, -6.5) * mm, "construction": true});
            skPoint(sketch, "E195.MirrorP", {"position": v(-371.6, 5.23) * mm});
            skLineSegment(sketch, "E196.MirrorCS", {"start": v(-351.1, 5.23) * mm, "end": v(-351.67, -5.65) * mm});
            skLineSegment(sketch, "E197", {"start": v(-330.1, -9.77) * mm, "end": v(-295.1, -9.77) * mm});
            skLineSegment(sketch, "E198", {"start": v(-420.1, -9.77) * mm, "end": v(-404.1, -9.77) * mm});
            skLineSegment(sketch, "E199", {"start": v(-295.1, -9.77) * mm, "end": v(-295.1, -5.65) * mm});
            skLineSegment(sketch, "E200", {"start": v(-295.1, -5.65) * mm, "end": v(-326.1, -5.65) * mm});
            skLineSegment(sketch, "E201", {"start": v(-424.1, -5.65) * mm, "end": v(-455.1, -5.65) * mm});
            skLineSegment(sketch, "E202", {"start": v(-455.1, -5.65) * mm, "end": v(-455.1, -9.77) * mm});
            skSolve(sketch);
        }
        {
            var Q0;
            {var subQ1=sQuery(id+"F10.wireOp",EDGE,"E126.right");Q0=makeQuery(id+"F10.imprint","IMPRINT",FACE,{"disambiguationData":[TD([[makeQuery(id+"F10.imprint","IMPRINT",EDGE,{"derivedFrom":subQ1}),-1.0]])]});}
            var Q1;
            {var subQ0=sQuery(id+"F10.wireOp",EDGE,"E126.left");Q1=makeQuery(id+"F10.imprint","IMPRINT",FACE,{"disambiguationData":[TD([[makeQuery(id+"F10.imprint","IMPRINT",EDGE,{"derivedFrom":subQ0}),1.0]])]});}
            extrude(context, id + "F11", {"entities" : qUnion([Q0, Q1]), "depth" : 25 * mm, "offsetDistance" : 25 * mm});
        }
        {
            var Q0;
            {var subQ8=sQuery(id+"F10.wireOp",EDGE,"E127");Q0=makeQuery(id+"F10.imprint","IMPRINT",FACE,{"disambiguationData":[TD([[makeQuery(id+"F10.imprint","IMPRINT",EDGE,{"derivedFrom":subQ8}),1.0]])]});}
            var Q1;
            {var subQ6=sQuery(id+"F10.wireOp",EDGE,"E134.MirrorCS");Q1=makeQuery(id+"F10.imprint","IMPRINT",FACE,{"disambiguationData":[TD([[makeQuery(id+"F10.imprint","IMPRINT",EDGE,{"derivedFrom":subQ6}),-1.0]])]});}
            extrude(context, id + "F12", {"entities" : qUnion([Q0, Q1]), "depth" : 30 * mm, "offsetDistance" : 25 * mm});
        }
        {
            var Q0;
            {var subQ0=sQuery(id+"F10.wireOp",EDGE,"E49.left");Q0=makeQuery(id+"F10.imprint","IMPRINT",FACE,{"disambiguationData":[TD([[makeQuery(id+"F10.imprint","IMPRINT",EDGE,{"derivedFrom":subQ0}),1.0]])]});}
            var Q1;
            {var subQ1=sQuery(id+"F10.wireOp",EDGE,"E49.right");Q1=makeQuery(id+"F10.imprint","IMPRINT",FACE,{"disambiguationData":[TD([[makeQuery(id+"F10.imprint","IMPRINT",EDGE,{"derivedFrom":subQ1}),-1.0]])]});}
            extrude(context, id + "F13", {"entities" : qUnion([Q0, Q1]), "depth" : 25 * mm, "offsetDistance" : 25 * mm});
        }
        {
            var Q0;
            {var subQ6=sQuery(id+"F10.wireOp",EDGE,"E50");Q0=makeQuery(id+"F10.imprint","IMPRINT",FACE,{"disambiguationData":[TD([[makeQuery(id+"F10.imprint","IMPRINT",EDGE,{"derivedFrom":subQ6}),1.0]])]});}
            var Q1;
            {var subQ7=sQuery(id+"F10.wireOp",EDGE,"E57.MirrorCS");Q1=makeQuery(id+"F10.imprint","IMPRINT",FACE,{"disambiguationData":[TD([[makeQuery(id+"F10.imprint","IMPRINT",EDGE,{"derivedFrom":subQ7}),-1.0]])]});}
            extrude(context, id + "F14", {"entities" : qUnion([Q0, Q1]), "depth" : 30 * mm, "offsetDistance" : 25 * mm});
        }
    });
